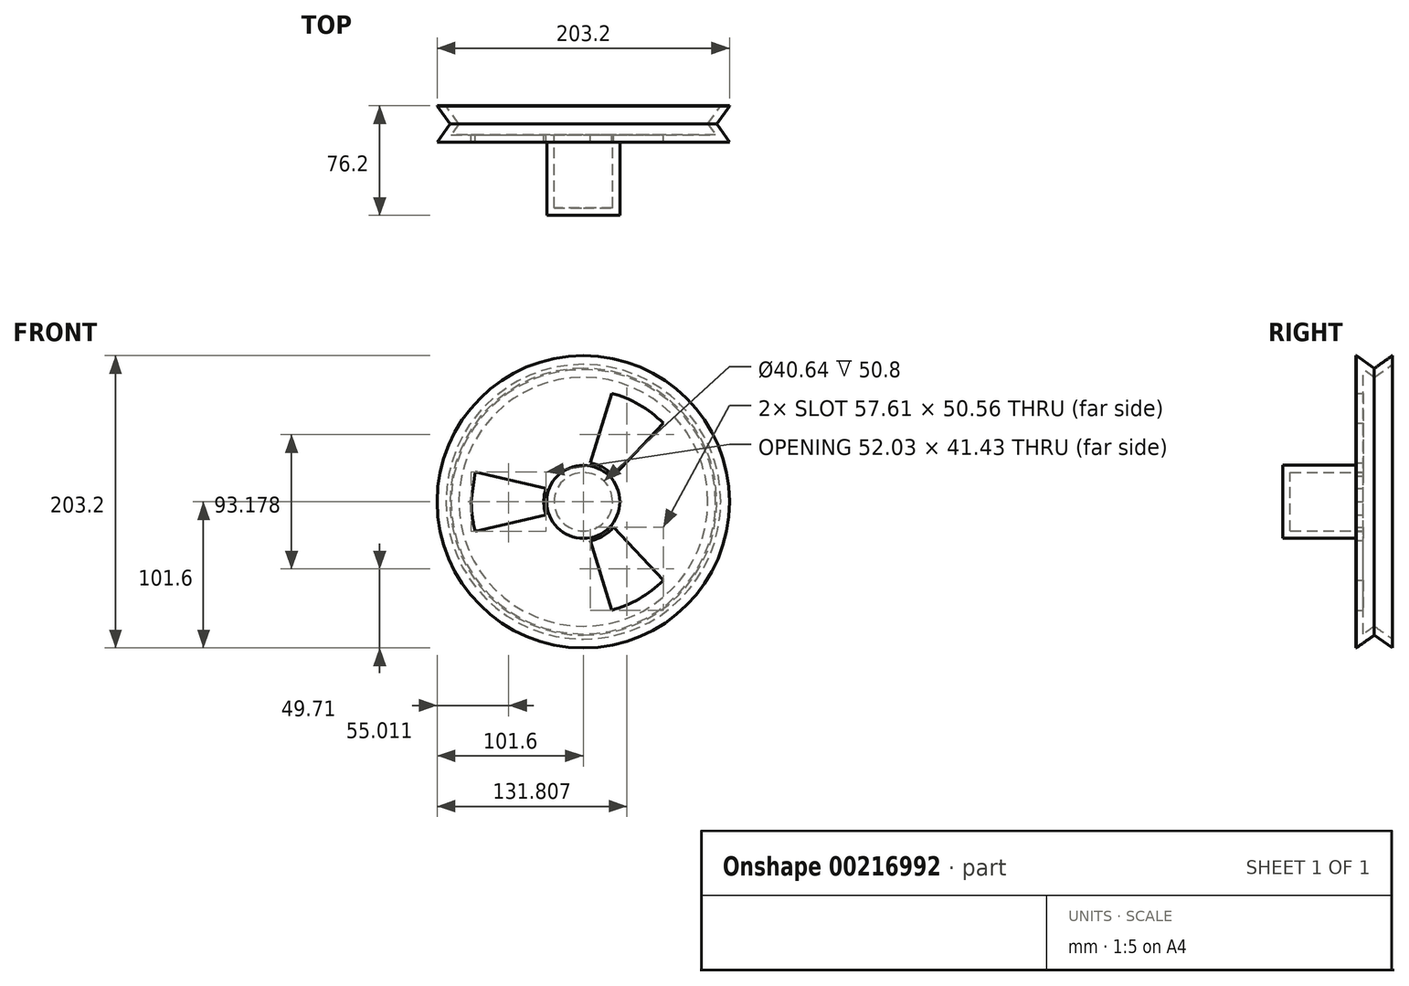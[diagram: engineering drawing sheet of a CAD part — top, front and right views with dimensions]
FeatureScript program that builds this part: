
annotation { "Feature Type Name" : "Feature", "Feature Type Description" : "" }
export const myFeature = defineFeature(function(context is Context, id is Id, definition is map)
    precondition{}
    {
        {
            var Q0;
            Q0=qCreatedBy(makeId("Front.planeOp"),FACE);
            var sketch = newSketch(context, id + "F0", { "sketchPlane" : qUnion([Q0])});
            skCircle(sketch, "E0", {"center": v(0, 0) * mm, "radius": 101.6 * mm});
            skSolve(sketch);
        }
        {
            var Q0;
            Q0=makeQuery(id+"F0.imprint","IMPRINT",FACE,{"disambiguationData":[TD([[makeQuery(id+"F0.imprint","IMPRINT",EDGE,{"derivedFrom":sQuery(id+"F0.wireOp",EDGE,"E0")}),1.0]])]});
            extrude(context, id + "F1", {"entities" : qUnion([Q0]), "depth" : 25.4 * mm});
        }
        {
            var Q0;
            Q0=qCreatedBy(makeId("Right.planeOp"),FACE);
            var sketch = newSketch(context, id + "F2", { "sketchPlane" : qUnion([Q0])});
            skLineSegment(sketch, "E1", {"start": v(0, 101.7) * mm, "end": v(-12.7, 101.7) * mm});
            skLineSegment(sketch, "E2", {"start": v(0, 101.7) * mm, "end": v(-12.7, 92.73) * mm});
            skLineSegment(sketch, "E3", {"start": v(-12.7, 92.73) * mm, "end": v(-25.44, 101.7) * mm});
            skLineSegment(sketch, "E4", {"start": v(-25.44, 101.7) * mm, "end": v(-12.7, 101.7) * mm});
            skSolve(sketch);
        }
        {
            var Q0;
            Q0 = qSketchRegion(id + "F2", true);
            var Q1;
            Q1=makeQuery(id+"F1.opExtrude","CAP_EDGE",EDGE,{"disambiguationData":[OSD([sQuery(id+"F0.wireOp",EDGE,"E0")])],"isStart":false});
            revolve(context, id + "F3", {"operationType" : NewBodyOperationType.REMOVE, "entities" : qUnion([Q0]), "axis" : qUnion([Q1]), "revolveType" : RevolveType.FULL, "oppositeDirection" : true});
        }
        {
            var Q0;
            Q0=makeQuery(id+"F1.opExtrude","CAP_FACE",FACE,{"disambiguationData":[OSD([sQuery(id+"F0.wireOp",EDGE,"E0")])],"isStart":false});
            var sketch = newSketch(context, id + "F4", { "sketchPlane" : qUnion([Q0])});
            skCircle(sketch, "E5", {"center": v(0, 0) * mm, "radius": 25.4 * mm});
            skSolve(sketch);
        }
        {
            var Q0;
            Q0 = qSketchRegion(id + "F4", true);
            extrude(context, id + "F5", {"entities" : qUnion([Q0]), "operationType" : NewBodyOperationType.ADD, "depth" : 50.8 * mm});
        }
        {
            var Q0;
            Q0=makeQuery(id+"F1.opExtrude","CAP_FACE",FACE,{"disambiguationData":[OSD([sQuery(id+"F0.wireOp",EDGE,"E0")])],"isStart":true});
            shell(context, id + "F6", {"entities" : qUnion([Q0]), "thickness" : 5.08 * mm});
        }
        {
            var Q0;
            Q0=makeQuery(id+"F6.opShell","OFFSET_FACE",FACE,{"disambiguationData":[OSD([sQuery(id+"F0.wireOp",EDGE,"E0")])]});
            var sketch = newSketch(context, id + "F7", { "sketchPlane" : qUnion([Q0])});
            skCircle(sketch, "E6", {"center": v(0, 0) * mm, "radius": 77.9 * mm});
            skCircle(sketch, "E7", {"center": v(0, 0) * mm, "radius": 27.48 * mm});
            skLineSegment(sketch, "E8", {"start": v(77.9, 0) * mm, "end": v(75.1, 20.71) * mm});
            skLineSegment(sketch, "E9", {"start": v(75.1, 20.71) * mm, "end": v(25.88, 9.25) * mm});
            skLineSegment(sketch, "E10.MirrorCS", {"start": v(75.1, -20.71) * mm, "end": v(25.88, -9.25) * mm});
            skPoint(sketch, "E11.start.orphan", {"position": v(27.48, 0) * mm});
            skLineSegment(sketch, "E12.1.0", {"start": v(-19.61, 75.4) * mm, "end": v(-4.93, 27.04) * mm});
            skLineSegment(sketch, "E12.1.1", {"start": v(-55.49, 54.68) * mm, "end": v(-20.95, 17.78) * mm});
            skLineSegment(sketch, "E12.2.0", {"start": v(-55.49, -54.68) * mm, "end": v(-20.95, -17.78) * mm});
            skLineSegment(sketch, "E12.2.1", {"start": v(-19.61, -75.4) * mm, "end": v(-4.93, -27.04) * mm});
            skSolve(sketch);
        }
        {
            var Q0;
            {var subQ0=sQuery(id+"F7.wireOp",EDGE,"E12.1.0");Q0=makeQuery(id+"F7.imprint","IMPRINT",FACE,{"disambiguationData":[TD([[makeQuery(id+"F7.imprint","IMPRINT",EDGE,{"derivedFrom":subQ0}),-1.0]])]});}
            var Q1;
            {var subQ0=sQuery(id+"F7.wireOp",EDGE,"E12.2.0");Q1=makeQuery(id+"F7.imprint","IMPRINT",FACE,{"disambiguationData":[TD([[makeQuery(id+"F7.imprint","IMPRINT",EDGE,{"derivedFrom":subQ0}),-1.0]])]});}
            var Q2;
            {var subQ1=sQuery(id+"F7.wireOp",EDGE,"E8");Q2=makeQuery(id+"F7.imprint","IMPRINT",FACE,{"disambiguationData":[TD([[makeQuery(id+"F7.imprint","IMPRINT",EDGE,{"derivedFrom":subQ1}),1.0]])]});}
            extrude(context, id + "F8", {"entities" : qUnion([Q0, Q1, Q2]), "operationType" : NewBodyOperationType.REMOVE, "endBound" : BoundingType.THROUGH_ALL, "oppositeDirection" : true, "depth" : 25.4 * mm});
        }
    });
